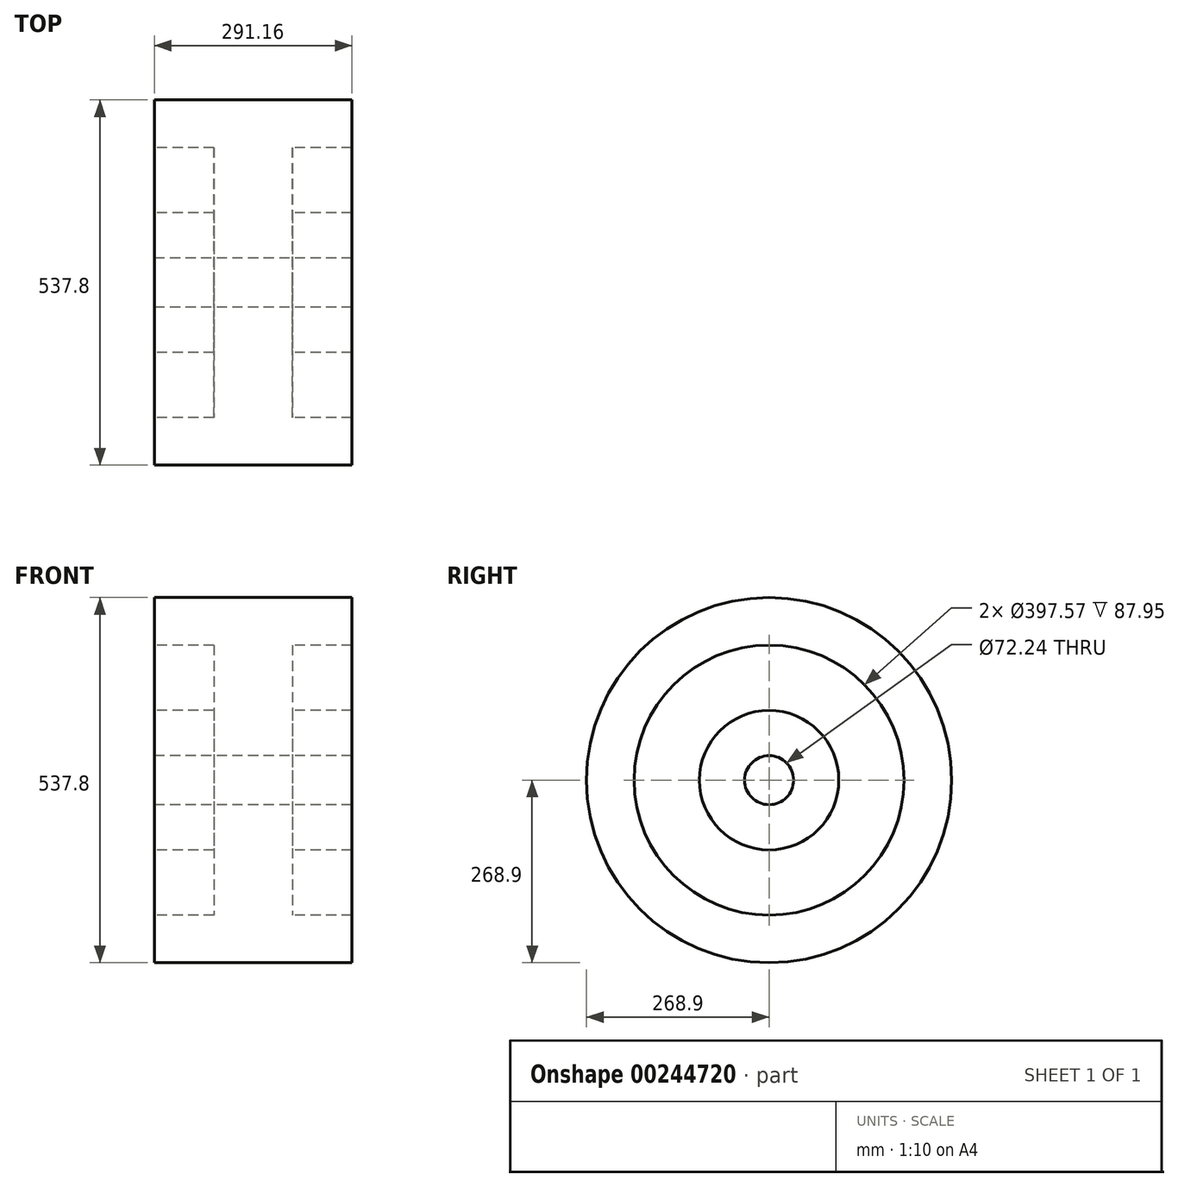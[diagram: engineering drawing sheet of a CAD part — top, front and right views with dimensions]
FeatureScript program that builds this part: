
annotation { "Feature Type Name" : "Feature", "Feature Type Description" : "" }
export const myFeature = defineFeature(function(context is Context, id is Id, definition is map)
    precondition{}
    {
        {
            var Q0;
            Q0=qCreatedBy(makeId("Front.planeOp"),FACE);
            var sketch = newSketch(context, id + "F0", { "sketchPlane" : qUnion([Q0])});
            skLineSegment(sketch, "E0", {"start": v(-242.5, 0) * mm, "end": v(234.76, 0) * mm, "construction": true});
            skLineSegment(sketch, "E1", {"start": v(-145.58, 36.12) * mm, "end": v(-145.58, 102.7) * mm});
            skLineSegment(sketch, "E2", {"start": v(-145.58, 102.7) * mm, "end": v(-57.63, 102.7) * mm});
            skLineSegment(sketch, "E3", {"start": v(-57.63, 102.7) * mm, "end": v(-57.63, 198.79) * mm});
            skLineSegment(sketch, "E4", {"start": v(-57.63, 198.79) * mm, "end": v(-145.58, 198.79) * mm});
            skLineSegment(sketch, "E5", {"start": v(-145.58, 198.79) * mm, "end": v(-145.58, 268.9) * mm});
            skLineSegment(sketch, "E6", {"start": v(-145.58, 268.9) * mm, "end": v(145.58, 268.9) * mm});
            skLineSegment(sketch, "E7", {"start": v(145.58, 268.9) * mm, "end": v(145.58, 198.79) * mm});
            skLineSegment(sketch, "E8", {"start": v(145.58, 198.79) * mm, "end": v(57.63, 198.79) * mm});
            skLineSegment(sketch, "E9", {"start": v(-145.58, 36.12) * mm, "end": v(145.58, 36.12) * mm});
            skLineSegment(sketch, "E10", {"start": v(145.58, 36.12) * mm, "end": v(145.58, 102.7) * mm});
            skLineSegment(sketch, "E11", {"start": v(57.63, 198.79) * mm, "end": v(57.63, 102.7) * mm});
            skLineSegment(sketch, "E12", {"start": v(57.63, 102.7) * mm, "end": v(145.58, 102.7) * mm});
            skLineSegment(sketch, "E13", {"start": v(0, 0) * mm, "end": v(0, 383.38) * mm, "construction": true});
            skSolve(sketch);
        }
        {
            var Q0;
            Q0 = qSketchRegion(id + "F0", true);
            var Q1;
            Q1=sQuery(id+"F0.wireOp",EDGE,"E0");
            revolve(context, id + "F1", {"entities" : qUnion([Q0]), "axis" : qUnion([Q1]), "revolveType" : RevolveType.FULL});
        }
    });
